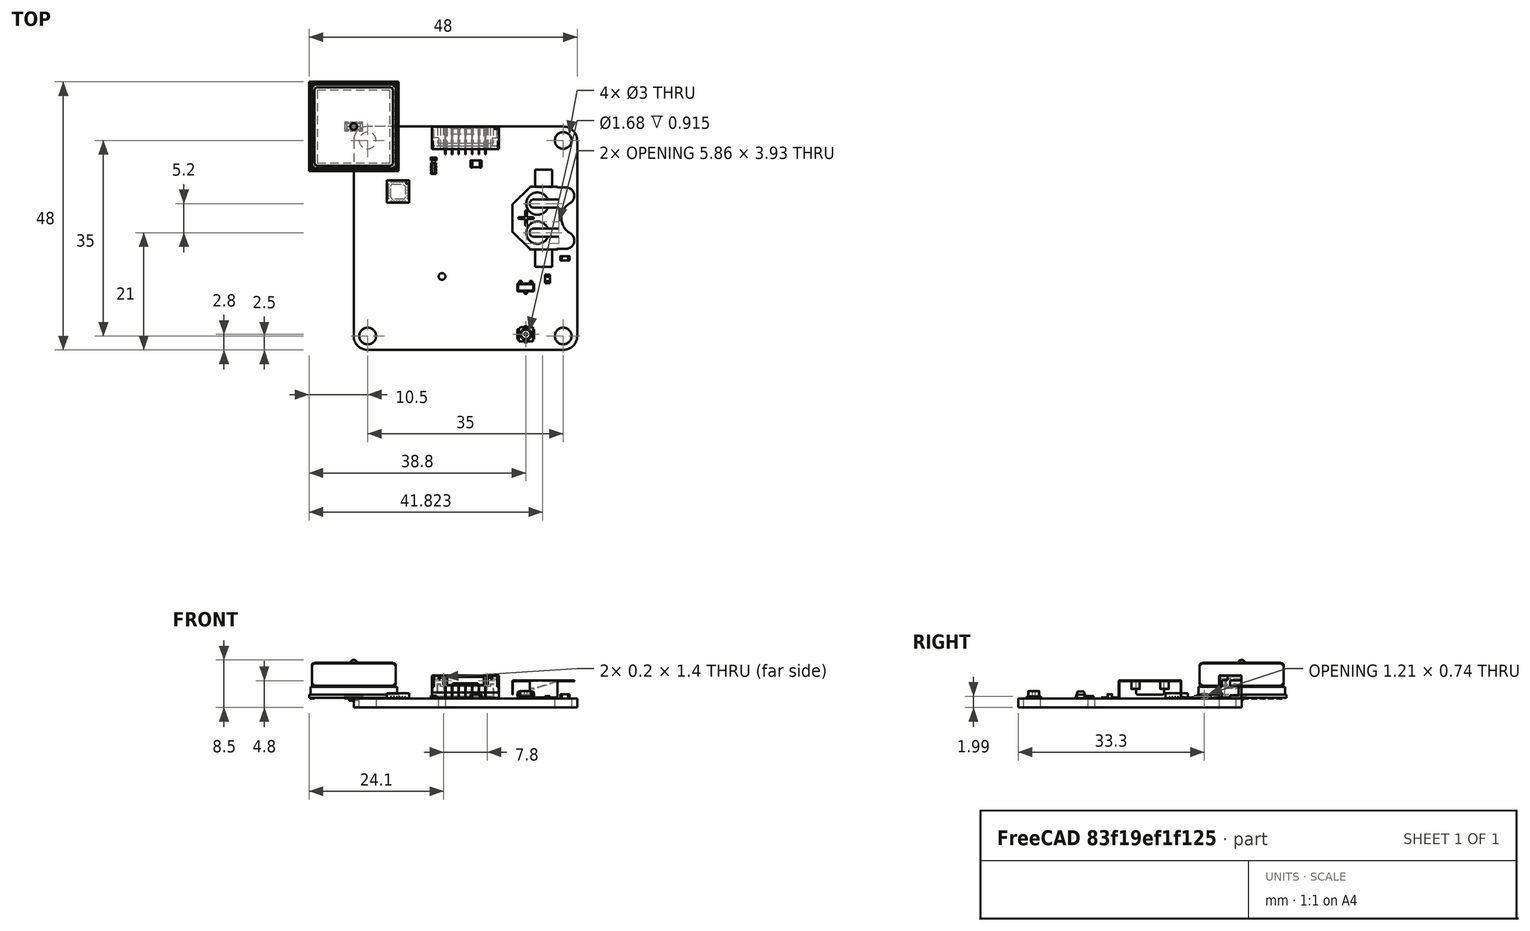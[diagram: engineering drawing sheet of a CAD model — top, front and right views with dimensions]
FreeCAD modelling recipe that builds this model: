
FCSTD DOCUMENT  (FreeCAD 0.19R)
Label: gps_v3
License: All rights reserved
LicenseURL: http://en.wikipedia.org/wiki/All_rights_reserved
objects: Part::Feature×40, App::Link×14, App::Part×7, PartDesign::CoordinateSystem×1, Sketcher::SketchObject×1
note: 42 computed .brp shape members not serialized (recipe doc carries the construction recipe); baked Part::Feature solids carry a one-line shape summary decoded from their .brp

FEATURE [PartDesign::CoordinateSystem] Local_CS_332e
  AttacherType = Attacher::AttachEngine3D
FEATURE [Part::Feature] Pcb_332e
  Placement = pos=(-100,100,0) rot=(0,0,1;0rad)
  shape: bbox 40 x 40 x 1.6 mm, 15 faces (baked)
FEATURE [Sketcher::SketchObject] PCB_Sketch_332e
  FullyConstrained = false
  sketch-geometry (8):
    g0: LineSegment StartX=37.5 StartY=6.7e-15 StartZ=0 EndX=2.5 EndY=-1.8e-15 EndZ=0
    g1: LineSegment StartX=40 StartY=-37.5 StartZ=0 EndX=40 EndY=-2.5 EndZ=0
    g2: LineSegment StartX=2.5 StartY=-40 StartZ=0 EndX=37.5 EndY=-40 EndZ=0
    g3: LineSegment StartX=1.8e-15 StartY=-2.5 StartZ=0 EndX=-6.7e-15 EndY=-37.5 EndZ=0
    g4: ArcOfCircle CenterX=37.5 CenterY=-2.5 CenterZ=0 NormalX=0 NormalY=0 NormalZ=1 AngleXU=0 Radius=2.5 StartAngle=0 EndAngle=1.5708
    g5: ArcOfCircle CenterX=37.5 CenterY=-37.5 CenterZ=0 NormalX=0 NormalY=0 NormalZ=1 AngleXU=0 Radius=2.5 StartAngle=4.71239 EndAngle=6.28319
    g6: ArcOfCircle CenterX=2.5 CenterY=-37.5 CenterZ=0 NormalX=0 NormalY=0 NormalZ=1 AngleXU=0 Radius=2.5 StartAngle=3.14159 EndAngle=4.71239
    g7: ArcOfCircle CenterX=2.5 CenterY=-2.5 CenterZ=0 NormalX=0 NormalY=0 NormalZ=1 AngleXU=0 Radius=2.5 StartAngle=1.5708 EndAngle=3.14159
  constraints (8):
    c: Coincident(g3,g6)
    c: Coincident(g3,g7)
    c: Coincident(g2,g6)
    c: Coincident(g0,g7)
    c: Coincident(g2,g5)
    c: Coincident(g0,g4)
    c: Coincident(g1,g5)
    c: Coincident(g1,g4)
FEATURE [App::Part] Board_Geoms_332e
  Group = -> [Local_CS_332e,Pcb_332e,PCB_Sketch_332e]
  Origin = -> Origin
FEATURE [Part::Feature] Shape  label="R5_R_0603_5F886D71"
  Placement = pos=(34.7,-27.3,0) rot=(0,0,-1;1.5708rad)
  shape: bbox 0.85 x 1.55 x 0.45 mm, 28 faces (baked)
FEATURE [App::Link] R5_R_0603_5F886D71_ln_  label="R4_R_0603_5F886374"
  LinkPlacement = pos=(32.5,-26.5,0) rot=(0,0,1;3.14159rad)
  LinkedObject = -> Shape
  Placement = pos=(32.5,-26.5,0) rot=(0,0,1;3.14159rad)
FEATURE [Part::Feature] Shape001  label="BT1_Battery_Retainer_5F86F5B3"
  Placement = pos=(33.492,-16.4,0) rot=(0,0,-1;1.5708rad)
  shape: bbox 11.1 x 17.4 x 3.12 mm, 94 faces (baked)
FEATURE [Part::Feature] Shape002  label="C1_C_0402_5F86F5BD"
  Placement = pos=(14.3,-5.8,0) rot=(0,0,1;3.14159rad)
  shape: bbox 1 x 0.5 x 0.5 mm, 28 faces (baked)
FEATURE [Part::Feature] Shape003  label="C2_C_0603_5F86F5C7"
  Placement = pos=(37.8,-23.6,0) rot=(0,0,1;3.14159rad)
  shape: bbox 1.6 x 0.81 x 0.78 mm, 28 faces (baked)
FEATURE [App::Link] C2_C_0603_5F86F5C7_ln_  label="C3_C_0603_5F86F5D1"
  LinkPlacement = pos=(4.5,-22.2,0) rot=(0,0,1;1.5708rad)
  LinkedObject = -> Shape003
  Placement = pos=(4.5,-22.2,0) rot=(0,0,1;1.5708rad)
FEATURE [App::Link] C2_C_0603_5F86F5C7_ln_001  label="C4_C_0603_5F86F5DB"
  LinkPlacement = pos=(5.9,-22.2,0) rot=(0,0,1;1.5708rad)
  LinkedObject = -> Shape003
  Placement = pos=(5.9,-22.2,0) rot=(0,0,1;1.5708rad)
FEATURE [App::Link] C2_C_0603_5F86F5C7_ln_002  label="C5_C_0603_5F86F5E5"
  LinkPlacement = pos=(31.6,-31.2,0) rot=(0,0,1;3.14159rad)
  LinkedObject = -> Shape003
  Placement = pos=(31.6,-31.2,0) rot=(0,0,1;3.14159rad)
FEATURE [App::Link] C2_C_0603_5F86F5C7_ln_003  label="C101_C_0603_5F86F5EF"
  LinkPlacement = pos=(21.9,-8.3,0) rot=(0,0,1;3.14159rad)
  LinkedObject = -> Shape003
  Placement = pos=(21.9,-8.3,0) rot=(0,0,1;3.14159rad)
FEATURE [Part::Feature] Shape004  label="C102_C_0805_5F86F5F9"
  Placement = pos=(21.9,-6.7,0) rot=(0,0,1;3.14159rad)
  shape: bbox 2 x 1.25 x 0.78 mm, 28 faces (baked)
FEATURE [App::Link] C2_C_0603_5F86F5C7_ln_004  label="C103_C_0603_5F86F603"
  LinkPlacement = pos=(4.1,-11.7,0) rot=(0,0,-1;1.5708rad)
  LinkedObject = -> Shape003
  Placement = pos=(4.1,-11.7,0) rot=(0,0,-1;1.5708rad)
FEATURE [Part::Feature] Part__Feature  label="Compound"
  shape: bbox 1.6 x 0.18 x 0.8 mm, 19 faces (baked)
FEATURE [Part::Feature] Part__Feature001  label="Compound001"
  shape: bbox 0.6 x 0.1 x 0.5 mm, 6 faces (baked)
FEATURE [App::Part] Compound  label="D1_Compound002_5F86F613"
  Group = -> [Part__Feature,Part__Feature001]
  Origin = -> Origin008
  Placement = pos=(30.5,-2.1,0) rot=(0.57735,0.57735,0.57735;2.0944rad)
FEATURE [App::Link] D1_Compound002_5F86F613_ln_  label="D101_Compound002_5F86F623"
  LinkPlacement = pos=(9.1,-2.1,0) rot=(0.57735,0.57735,0.57735;2.0944rad)
  LinkedObject = -> Compound
  Placement = pos=(9.1,-2.1,0) rot=(0.57735,0.57735,0.57735;2.0944rad)
FEATURE [App::Link] R5_R_0603_5F886D71_ln_001  label="L1_R_0603_5F86F62D"
  LinkPlacement = pos=(4.6,-19.2,0) rot=(0,0,1;1.5708rad)
  LinkedObject = -> Shape
  Placement = pos=(4.6,-19.2,0) rot=(0,0,1;1.5708rad)
FEATURE [Part::Feature] Shape005  label="P101_BrickletConn_7pin_5F86F64F"
  Placement = pos=(20,-2.54,0) rot=(0,0,1;3.14159rad)
  shape: bbox 12 x 4.98 x 4.1 mm, 457 faces (baked)
FEATURE [Part::Feature] Shape006  label="P104_U-FL_5F86F666"
  Placement = pos=(30.8,-37.2,0) rot=(0,0,1;3.14159rad)
  shape: bbox 3 x 2.85 x 1.34 mm, 33 faces (baked)
FEATURE [Part::Feature] Shape007  label="Q1_SOT23_5F86F671"
  Placement = pos=(30.8,-28.8,0) rot=(0,0,1;3.14159rad)
  shape: bbox 3 x 2.251 x 1.223 mm, 49 faces (baked)
FEATURE [App::Link] R5_R_0603_5F886D71_ln_002  label="R1_R_0603_5F86F67B"
  LinkPlacement = pos=(3.2,-21.4,0) rot=(0,0,1;1.5708rad)
  LinkedObject = -> Shape
  Placement = pos=(3.2,-21.4,0) rot=(0,0,1;1.5708rad)
FEATURE [App::Link] R5_R_0603_5F886D71_ln_003  label="R2_R_0603_5F86F685"
  LinkPlacement = pos=(4.2,-31.5,0) rot=(0,0,-1;1.5708rad)
  LinkedObject = -> Shape
  Placement = pos=(4.2,-31.5,0) rot=(0,0,-1;1.5708rad)
FEATURE [App::Link] R5_R_0603_5F886D71_ln_004  label="R3_R_0603_5F86F68F"
  LinkPlacement = pos=(2.8,-31.5,0) rot=(0,0,-1;1.5708rad)
  LinkedObject = -> Shape
  Placement = pos=(2.8,-31.5,0) rot=(0,0,-1;1.5708rad)
FEATURE [Part::Feature] Shape008  label="RP1_Cut_5F86F69F"
  Placement = pos=(14.3,-7.5,0) rot=(0,0,1;0rad)
  shape: bbox 0.96 x 2 x 0.41 mm, 110 faces (baked)
FEATURE [Part::Feature] Part__Feature002  label="Compound002"
  shape: bbox 1.38 x 0.4873 x 0.06 mm, 101 faces (baked)
FEATURE [Part::Feature] Part__Feature003  label="Compound003"
  shape: bbox 3.2 x 1 x 0.1 mm, 91 faces (baked)
FEATURE [Part::Feature] Part__Feature004  label="Compound004"
  shape: bbox 3.2 x 1.5 x 0.35 mm, 30 faces (baked)
FEATURE [Part::Feature] Part__Feature005  label="Compound005"
  shape: bbox 3.2 x 1.6 x 0.45 mm, 126 faces (baked)
FEATURE [App::Part] Compound001  label="RP2_Compound006_5F86F6AF"
  Group = -> [Part__Feature002,Part__Feature003,Part__Feature004,Part__Feature005]
  Origin = -> Origin009
  Placement = pos=(7.9,-6.6,0) rot=(0,0,1;3.14159rad)
FEATURE [App::Link] RP2_Compound006_5F86F6AF_ln_  label="RP3_Compound006_5F86F6BF"
  LinkPlacement = pos=(21.4,-15.1,0) rot=(0,0,1;0rad)
  LinkedObject = -> Compound001
  Placement = pos=(21.4,-15.1,0) rot=(0,0,1;0rad)
FEATURE [Part::Feature] Part__Feature006  label="PA1616D"
  shape: bbox 15 x 15 x 4.8 mm, 42 faces (baked)
FEATURE [Part::Feature] Part__Feature007  label="PA1616D001"
  shape: bbox 15.5 x 15.5 x 1.4 mm, 6 faces (baked)
FEATURE [Part::Feature] Part__Feature008  label="PA1616D002"
  shape: bbox 16 x 16 x 0.6 mm, 6 faces (baked)
FEATURE [Part::Feature] Part__Feature009  label="PA1616D003"
  shape: bbox 0.8 x 1 x 0.1 mm, 6 faces (baked)
FEATURE [Part::Feature] Part__Feature010  label="PA1616D004"
  shape: bbox 0.8 x 1 x 0.1 mm, 6 faces (baked)
FEATURE [Part::Feature] Part__Feature011  label="PA1616D005"
  shape: bbox 0.8 x 1 x 0.1 mm, 6 faces (baked)
FEATURE [Part::Feature] Part__Feature012  label="PA1616D006"
  shape: bbox 0.8 x 1 x 0.1 mm, 6 faces (baked)
FEATURE [Part::Feature] Part__Feature013  label="PA1616D007"
  shape: bbox 0.8 x 1 x 0.1 mm, 6 faces (baked)
FEATURE [Part::Feature] Part__Feature014  label="PA1616D008"
  shape: bbox 0.8 x 1 x 0.1 mm, 6 faces (baked)
FEATURE [Part::Feature] Part__Feature015  label="PA1616D009"
  shape: bbox 0.8 x 1 x 0.1 mm, 6 faces (baked)
FEATURE [Part::Feature] Part__Feature016  label="PA1616D010"
  shape: bbox 0.8 x 1 x 0.1 mm, 6 faces (baked)
FEATURE [Part::Feature] Part__Feature017  label="PA1616D011"
  shape: bbox 0.8 x 1 x 0.1 mm, 6 faces (baked)
FEATURE [Part::Feature] Part__Feature018  label="PA1616D012"
  shape: bbox 0.8 x 1 x 0.1 mm, 6 faces (baked)
FEATURE [Part::Feature] Part__Feature019  label="PA1616D013"
  shape: bbox 0.8 x 1 x 0.1 mm, 6 faces (baked)
FEATURE [Part::Feature] Part__Feature020  label="PA1616D014"
  shape: bbox 0.8 x 1 x 0.1 mm, 6 faces (baked)
FEATURE [Part::Feature] Part__Feature021  label="PA1616D015"
  shape: bbox 0.8 x 1 x 0.1 mm, 6 faces (baked)
FEATURE [Part::Feature] Part__Feature022  label="PA1616D016"
  shape: bbox 0.8 x 1 x 0.1 mm, 6 faces (baked)
FEATURE [Part::Feature] Part__Feature023  label="PA1616D017"
  shape: bbox 0.8 x 1 x 0.1 mm, 6 faces (baked)
FEATURE [Part::Feature] Part__Feature024  label="PA1616D018"
  shape: bbox 0.8 x 1 x 0.1 mm, 6 faces (baked)
FEATURE [Part::Feature] Part__Feature025  label="PA1616D019"
  shape: bbox 0.8 x 1 x 0.1 mm, 6 faces (baked)
FEATURE [Part::Feature] Part__Feature026  label="PA1616D020"
  shape: bbox 0.8 x 1 x 0.1 mm, 6 faces (baked)
FEATURE [Part::Feature] Part__Feature027  label="PA1616D021"
  shape: bbox 0.8 x 1 x 0.1 mm, 6 faces (baked)
FEATURE [Part::Feature] Part__Feature028  label="PA1616D022"
  shape: bbox 0.8 x 1 x 0.1 mm, 6 faces (baked)
FEATURE [App::Part] PA1616D  label="U1_PA1616D023_5F86F6DE"
  Group = -> [Part__Feature006,Part__Feature007,Part__Feature008,Part__Feature009,Part__Feature010,Part__Feature011,Part__Feature012,Part__Feature013,Part__Feature014,Part__Feature015,Part__Feature016,Part__Feature017,Part__Feature018,Part__Feature019,Part__Feature020,Part__Feature021,Part__Feature022,Part__Feature023,Part__Feature024,Part__Feature025,Part__Feature026,Part__Feature027,Part__Feature028]
  Origin = -> Origin010
  Placement = pos=(15.8,-27.3,0) rot=(0,0,1;0rad)
FEATURE [Part::Feature] Shape009  label="U101_QFN-24_4x4mm_Pitch0.5mm_5F86F703"
  Placement = pos=(7.95,-11.65,0) rot=(-0.57735,0.57735,0.57735;4.18879rad)
  shape: bbox 4.02 x 4.02 x 0.9 mm, 173 faces (baked)
FEATURE [App::Link] C2_C_0603_5F86F5C7_ln_005  label="C6_C_0603_5F87FD12"
  LinkPlacement = pos=(30.7,-23.4,0) rot=(0,0,1;3.14159rad)
  LinkedObject = -> Shape003
  Placement = pos=(30.7,-23.4,0) rot=(0,0,1;3.14159rad)
FEATURE [App::Link] R5_R_0603_5F886D71_ln_005  label="L3_R_0603_5F87FD1C"
  LinkPlacement = pos=(29.9,-25.6,0) rot=(0,0,1;1.5708rad)
  LinkedObject = -> Shape
  Placement = pos=(29.9,-25.6,0) rot=(0,0,1;1.5708rad)
FEATURE [App::Part] Top_332e
  Group = -> [Shape,R5_R_0603_5F886D71_ln_,Shape001,Shape002,Shape003,C2_C_0603_5F86F5C7_ln_,C2_C_0603_5F86F5C7_ln_001,C2_C_0603_5F86F5C7_ln_002,C2_C_0603_5F86F5C7_ln_003,Shape004,C2_C_0603_5F86F5C7_ln_004,Compound,D1_Compound002_5F86F613_ln_,R5_R_0603_5F886D71_ln_001,Shape005,Shape006,Shape007,R5_R_0603_5F886D71_ln_002,R5_R_0603_5F886D71_ln_003,R5_R_0603_5F886D71_ln_004,Shape008,Compound001,+5 more]
  Origin = -> Origin003
FEATURE [App::Part] Step_Models_332e
  Group = -> [Top_332e]
  Origin = -> Origin002
FEATURE [App::Part] Board_332e  label="gps-v3"
  Group = -> [Board_Geoms_332e,Step_Models_332e]
  Origin = -> Origin001
